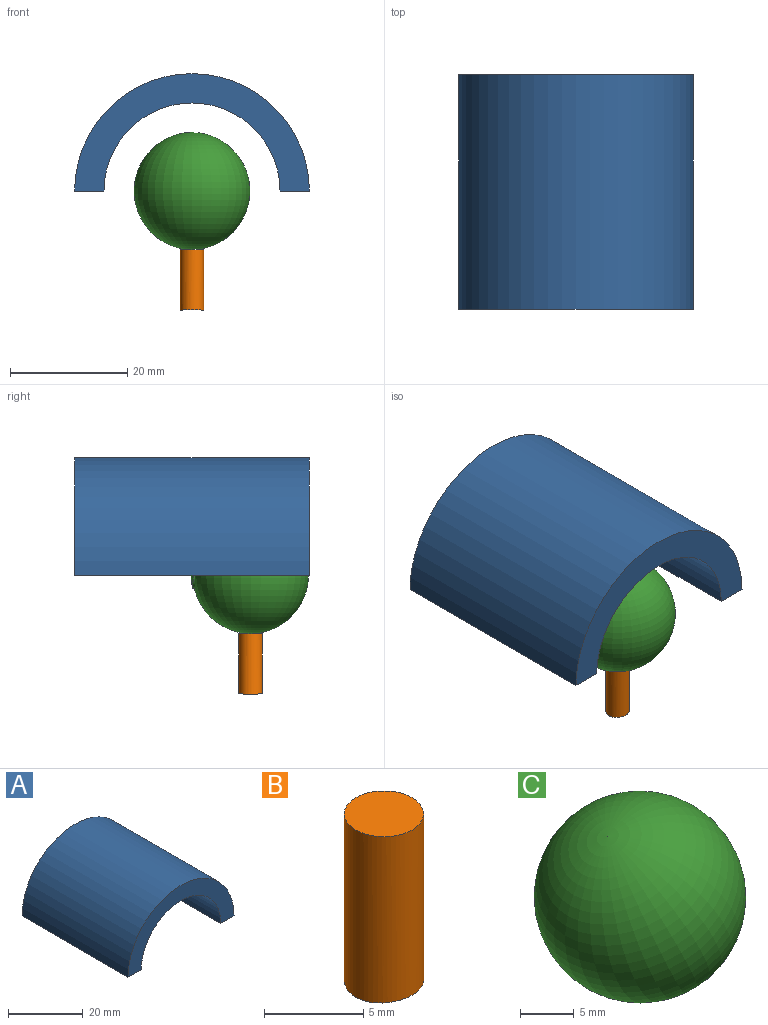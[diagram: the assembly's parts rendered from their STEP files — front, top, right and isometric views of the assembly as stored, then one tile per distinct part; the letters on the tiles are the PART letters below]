
ASSEMBLY  parts=3 mates=2
PART A: 12 faces, bbox 40x40x20 mm
  f0: cylinder r=15mm len=40mm, axis (0,1,0), area 1885mm2, adj f1,f3,f4,f5
  f1: plane 40x5mm, normal (0,0,-1), area 200mm2, adj f0,f2,f4,f5
  f2: cylinder r=20mm len=40mm, axis (0,1,0), area 2513.3mm2, adj f1,f3,f4,f5
  f3: plane 40x5mm, normal (0,0,-1), area 200mm2, adj f0,f2,f4,f5
  f4: plane 40x20mm, normal (0,-1,0), area 274.9mm2, adj f0,f1,f2,f3
  f5: plane 40x20mm, normal (0,1,0), area 269.6mm2, adj f0,f1,f2,f3,f6,f8,f10
  f6: cylinder r=0.75mm len=17.7mm, axis (0,1,0), area 83.4mm2, adj f5,f7
  f7: plane 1.5x1.5mm, normal (0,1,0), area 1.8mm2, adj f6
  f8: cylinder r=0.75mm len=17.7mm, axis (0,1,0), area 83.4mm2, adj f5,f9
  f9: plane 1.5x1.5mm, normal (0,1,0), area 1.8mm2, adj f8
  f10: cylinder r=0.75mm len=17.7mm, axis (0,1,0), area 83.4mm2, adj f5,f11
  f11: plane 1.5x1.5mm, normal (0,1,0), area 1.8mm2, adj f10
PART B: 3 faces, bbox 4x4x10.3 mm
  f0: cylinder r=2mm len=10.33mm, axis (0,0,-1), area 129mm2, adj f1,f2
  f1: plane 4x4mm, normal (0,0,1), area 12.6mm2, adj f0
  f2: cylinder r=15mm len=4mm, axis (0,1,0), area 12.6mm2, adj f0
PART C: 4 faces, bbox 14.1x16.4x19 mm
  f0: torus R=0.15mm, axis (-0.43,0,0.9), area 1227.5mm2
  f1: torus R=0.15mm, axis (-0.43,0,0.9), area 16.9mm2, adj f2
  f2: cylinder r=2.3mm len=16.25mm, axis (0,-1,0), area 233.9mm2, adj f1,f3
  f3: plane 4.6x4.6mm, normal (0,-1,0), area 16.6mm2, adj f2
PLACE A t=(-3.35,-0.88,46.78)mm
PLACE B t=(-3.35,0,11.58)mm
PLACE C rot(axis=(0,1,0),25.3deg) t=(1.25,-30.88,3.68)mm
MATE fastened B.f0 <-> C.f0  axis (0,0,1) through (-3.35,-30.88,36.78)mm
MATE fastened A.f1 <-> C.f0  axis (0,0,1) through (-3.35,-30.88,46.78)mm
